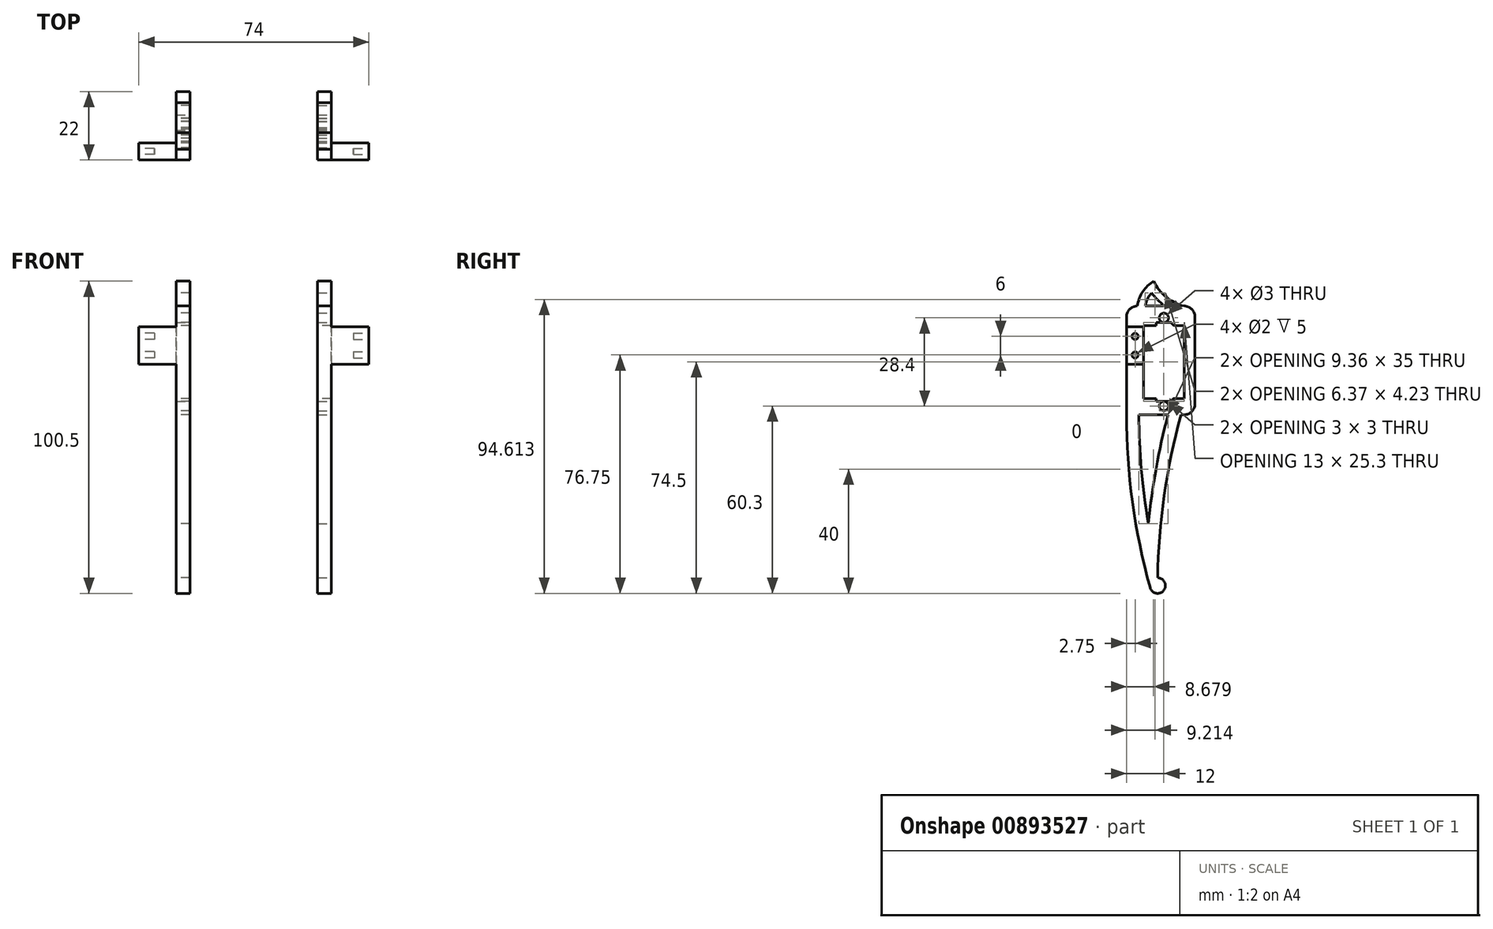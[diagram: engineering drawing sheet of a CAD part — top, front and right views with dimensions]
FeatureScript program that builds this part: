
annotation { "Feature Type Name" : "Feature", "Feature Type Description" : "" }
export const myFeature = defineFeature(function(context is Context, id is Id, definition is map)
    precondition{}
    {
        {
            var Q0;
            Q0=qCreatedBy(makeId("Right.planeOp"),FACE);
            var sketch = newSketch(context, id + "F0", { "sketchPlane" : qUnion([Q0])});
            skLineSegment(sketch, "E0.bottom", {"start": v(11, -17.5) * mm, "end": v(-11, -17.5) * mm});
            skLineSegment(sketch, "E0.top", {"start": v(11, 17.5) * mm, "end": v(-11, 17.5) * mm});
            skLineSegment(sketch, "E0.left", {"start": v(11, -17.5) * mm, "end": v(11, 17.5) * mm});
            skLineSegment(sketch, "E0.right", {"start": v(-11, -17.5) * mm, "end": v(-11, 17.5) * mm});
            skPoint(sketch, "E0.middle", {"position": v(0, 0) * mm});
            skSolve(sketch);
        }
        {
            var Q0;
            Q0 = qSketchRegion(id + "F0", true);
            extrude(context, id + "F1", {"entities" : qUnion([Q0]), "depth" : 4.5 * mm, "offsetDistance" : 25 * mm});
        }
        {
            var Q0;
            Q0=qCreatedBy(makeId("Right.planeOp"),FACE);
            var sketch = newSketch(context, id + "F2", { "sketchPlane" : qUnion([Q0])});
            skCircle(sketch, "E1", {"center": v(-1, -72.5) * mm, "radius": 2.5 * mm});
            skLineSegment(sketch, "E2.0", {"start": v(11, -17.5) * mm, "end": v(-11, -17.5) * mm});
            skArc(sketch, "E3", {"start": v(-11, -17.5) * mm, "mid": v(-9.1, -45.6) * mm, "end": v(-3.4, -73.17) * mm});
            skArc(sketch, "E4", {"start": v(6.5, -17.5) * mm, "mid": v(1.14, -43.52) * mm, "end": v(-1, -70) * mm});
            skLineSegment(sketch, "E5", {"start": v(-1, -70) * mm, "end": v(-1, -72.5) * mm, "construction": true});
            skArc(sketch, "E6.0", {"start": v(-7, -17.5) * mm, "mid": v(-6.24, -35.07) * mm, "end": v(-3.97, -52.5) * mm});
            skArc(sketch, "E7.0", {"start": v(2.36, -17.5) * mm, "mid": v(-1.51, -34.87) * mm, "end": v(-3.97, -52.5) * mm});
            skSolve(sketch);
        }
        {
            var Q0;
            {var subQ0=sQuery(id+"F2.wireOp",EDGE,"E3");Q0=makeQuery(id+"F2.imprint","IMPRINT",FACE,{"disambiguationData":[TD([[makeQuery(id+"F2.imprint","IMPRINT",EDGE,{"derivedFrom":subQ0}),1.0]])]});}
            var Q1;
            {var subQ0=sQuery(id+"F2.wireOp",EDGE,"E1");var subQ1=makeQuery(id+"F2.imprint","INTERSECT",VERTEX,{"derivedFrom":[subQ0,sQuery(id+"F2.wireOp",EDGE,"E3")]});Q1=makeQuery(id+"F2.imprint","IMPRINT",FACE,{"disambiguationData":[TD([[makeQuery(id+"F2.imprint","IMPRINT",EDGE,{"disambiguationData":[TD([[subQ1,1.0]])],"derivedFrom":subQ0}),1.0]])]});}
            var Q2;
            Q2=makeQuery(id+"F1.opExtrude","CAP_FACE",FACE,{"disambiguationData":[OSD([sQuery(id+"F0.wireOp",EDGE,"E0.bottom"),sQuery(id+"F0.wireOp",EDGE,"E0.top"),sQuery(id+"F0.wireOp",EDGE,"E0.left"),sQuery(id+"F0.wireOp",EDGE,"E0.right")])],"isStart":false});
            extrude(context, id + "F3", {"entities" : qUnion([Q0, Q1]), "operationType" : NewBodyOperationType.ADD, "endBound" : BoundingType.UP_TO_SURFACE, "depth" : 25 * mm, "endBoundEntityFace" : qUnion([Q2]), "offsetDistance" : 25 * mm});
        }
        {
            var Q0;
            Q0=makeQuery(id+"F1.opExtrude","SWEPT_EDGE",EDGE,{"disambiguationData":[OSD([sQuery(id+"F0.wireOp",EDGE,"E0.top"),sQuery(id+"F0.wireOp",EDGE,"E0.right")])]});
            var Q1;
            Q1=makeQuery(id+"F1.opExtrude","SWEPT_EDGE",EDGE,{"disambiguationData":[OSD([sQuery(id+"F0.wireOp",EDGE,"E0.top"),sQuery(id+"F0.wireOp",EDGE,"E0.left")])]});
            var Q2;
            Q2=makeQuery(id+"F1.opExtrude","SWEPT_EDGE",EDGE,{"disambiguationData":[OSD([sQuery(id+"F0.wireOp",EDGE,"E0.bottom"),sQuery(id+"F0.wireOp",EDGE,"E0.left")])]});
            fillet(context, id + "F4", {"entities" : qUnion([Q0, Q1, Q2]), "radius" : 3.5 * mm, "tangentPropagation" : true, "allowEdgeOverflow" : false});
        }
        {
            var Q0;
            Q0=qCreatedBy(makeId("Right.planeOp"),FACE);
            var sketch = newSketch(context, id + "F5", { "sketchPlane" : qUnion([Q0])});
            skLineSegment(sketch, "E8.0", {"start": v(7.5, 17.5) * mm, "end": v(-7.5, 17.5) * mm});
            skArc(sketch, "E9", {"start": v(-2.25, 25.5) * mm, "mid": v(1.7, 20.38) * mm, "end": v(7.5, 17.5) * mm});
            skArc(sketch, "E10", {"start": v(-2.25, 25.5) * mm, "mid": v(-5.8, 22.1) * mm, "end": v(-7.5, 17.5) * mm});
            skArc(sketch, "E11.0", {"start": v(-2.94, 21.73) * mm, "mid": v(-4.25, 19.76) * mm, "end": v(-4.97, 17.5) * mm});
            skArc(sketch, "E11.1", {"start": v(-2.94, 21.73) * mm, "mid": v(-0.96, 19.42) * mm, "end": v(1.4, 17.5) * mm});
            skSolve(sketch);
        }
        {
            var Q0;
            {var subQ1=sQuery(id+"F5.wireOp",EDGE,"E9");Q0=makeQuery(id+"F5.imprint","IMPRINT",FACE,{"disambiguationData":[TD([[makeQuery(id+"F5.imprint","IMPRINT",EDGE,{"derivedFrom":subQ1}),-1.0]])]});}
            var Q1;
            Q1=makeQuery(id+"F3.boolean.opBoolean","MERGE",FACE,{"derivedFrom":[makeQuery(id+"F1.opExtrude","CAP_FACE",FACE,{"disambiguationData":[OSD([sQuery(id+"F0.wireOp",EDGE,"E0.bottom"),sQuery(id+"F0.wireOp",EDGE,"E0.top"),sQuery(id+"F0.wireOp",EDGE,"E0.left"),sQuery(id+"F0.wireOp",EDGE,"E0.right")])],"isStart":false}),makeQuery(id+"F3.opExtrude","CAP_FACE",FACE,{"disambiguationData":[OSD([sQuery(id+"F2.wireOp",EDGE,"E1"),sQuery(id+"F2.wireOp",EDGE,"E2.0"),sQuery(id+"F2.wireOp",EDGE,"E3"),sQuery(id+"F2.wireOp",EDGE,"E4"),sQuery(id+"F2.wireOp",EDGE,"E6.0"),sQuery(id+"F2.wireOp",EDGE,"E7.0")])],"isStart":false})]});
            extrude(context, id + "F6", {"entities" : qUnion([Q0]), "operationType" : NewBodyOperationType.ADD, "endBound" : BoundingType.UP_TO_SURFACE, "depth" : 25 * mm, "endBoundEntityFace" : qUnion([Q1]), "offsetDistance" : 25 * mm});
        }
        {
            var Q0;
            Q0=makeQuery(id+"F6.boolean.opBoolean","MERGE",FACE,{"derivedFrom":[makeQuery(id+"F3.boolean.opBoolean","MERGE",FACE,{"derivedFrom":[makeQuery(id+"F1.opExtrude","CAP_FACE",FACE,{"disambiguationData":[OSD([sQuery(id+"F0.wireOp",EDGE,"E0.bottom"),sQuery(id+"F0.wireOp",EDGE,"E0.top"),sQuery(id+"F0.wireOp",EDGE,"E0.left"),sQuery(id+"F0.wireOp",EDGE,"E0.right")])],"isStart":true}),makeQuery(id+"F3.opExtrude","CAP_FACE",FACE,{"disambiguationData":[OSD([sQuery(id+"F2.wireOp",EDGE,"E1"),sQuery(id+"F2.wireOp",EDGE,"E2.0"),sQuery(id+"F2.wireOp",EDGE,"E3"),sQuery(id+"F2.wireOp",EDGE,"E4"),sQuery(id+"F2.wireOp",EDGE,"E6.0"),sQuery(id+"F2.wireOp",EDGE,"E7.0")])],"isStart":true})]}),makeQuery(id+"F6.opExtrude","CAP_FACE",FACE,{"disambiguationData":[OSD([sQuery(id+"F5.wireOp",EDGE,"E8.0"),sQuery(id+"F5.wireOp",EDGE,"E9"),sQuery(id+"F5.wireOp",EDGE,"E10"),sQuery(id+"F5.wireOp",EDGE,"E11.0"),sQuery(id+"F5.wireOp",EDGE,"E11.1")])],"isStart":true})]});
            var sketch = newSketch(context, id + "F7", { "sketchPlane" : qUnion([Q0])});
            skLineSegment(sketch, "E12.bottom", {"start": v(11, 10.75) * mm, "end": v(5.5, 10.75) * mm});
            skLineSegment(sketch, "E12.top", {"start": v(11, -1.25) * mm, "end": v(5.5, -1.25) * mm});
            skLineSegment(sketch, "E12.left", {"start": v(11, 10.75) * mm, "end": v(11, -1.25) * mm});
            skLineSegment(sketch, "E12.right", {"start": v(5.5, 10.75) * mm, "end": v(5.5, -1.25) * mm});
            skSolve(sketch);
        }
        {
            var Q0;
            Q0 = qSketchRegion(id + "F7", true);
            extrude(context, id + "F8", {"entities" : qUnion([Q0]), "operationType" : NewBodyOperationType.ADD, "depth" : 12 * mm, "offsetDistance" : 25 * mm});
        }
        {
            var Q0;
            Q0=makeQuery(id+"F6.boolean.opBoolean","MERGE",FACE,{"derivedFrom":[makeQuery(id+"F3.boolean.opBoolean","MERGE",FACE,{"derivedFrom":[makeQuery(id+"F1.opExtrude","CAP_FACE",FACE,{"disambiguationData":[OSD([sQuery(id+"F0.wireOp",EDGE,"E0.bottom"),sQuery(id+"F0.wireOp",EDGE,"E0.top"),sQuery(id+"F0.wireOp",EDGE,"E0.left"),sQuery(id+"F0.wireOp",EDGE,"E0.right")])],"isStart":true}),makeQuery(id+"F3.opExtrude","CAP_FACE",FACE,{"disambiguationData":[OSD([sQuery(id+"F2.wireOp",EDGE,"E1"),sQuery(id+"F2.wireOp",EDGE,"E2.0"),sQuery(id+"F2.wireOp",EDGE,"E3"),sQuery(id+"F2.wireOp",EDGE,"E4"),sQuery(id+"F2.wireOp",EDGE,"E6.0"),sQuery(id+"F2.wireOp",EDGE,"E7.0")])],"isStart":true})]}),makeQuery(id+"F6.opExtrude","CAP_FACE",FACE,{"disambiguationData":[OSD([sQuery(id+"F5.wireOp",EDGE,"E8.0"),sQuery(id+"F5.wireOp",EDGE,"E9"),sQuery(id+"F5.wireOp",EDGE,"E10"),sQuery(id+"F5.wireOp",EDGE,"E11.0"),sQuery(id+"F5.wireOp",EDGE,"E11.1")])],"isStart":true})]});
            var sketch = newSketch(context, id + "F9", { "sketchPlane" : qUnion([Q0])});
            skLineSegment(sketch, "E13.bottom", {"start": v(5.5, 11.25) * mm, "end": v(-7.5, 11.25) * mm});
            skLineSegment(sketch, "E13.top", {"start": v(5.5, -12.25) * mm, "end": v(-7.5, -12.25) * mm});
            skLineSegment(sketch, "E13.left", {"start": v(5.5, 11.25) * mm, "end": v(5.5, -12.25) * mm});
            skLineSegment(sketch, "E13.right", {"start": v(-7.5, 11.25) * mm, "end": v(-7.5, -12.25) * mm});
            skSolve(sketch);
        }
        {
            var Q0;
            Q0 = qSketchRegion(id + "F9", true);
            extrude(context, id + "F10", {"entities" : qUnion([Q0]), "operationType" : NewBodyOperationType.REMOVE, "oppositeDirection" : true, "depth" : 25 * mm, "offsetDistance" : 25 * mm});
        }
        {
            var Q0;
            Q0=makeQuery(id+"F6.boolean.opBoolean","MERGE",FACE,{"derivedFrom":[makeQuery(id+"F3.boolean.opBoolean","MERGE",FACE,{"derivedFrom":[makeQuery(id+"F1.opExtrude","CAP_FACE",FACE,{"disambiguationData":[OSD([sQuery(id+"F0.wireOp",EDGE,"E0.bottom"),sQuery(id+"F0.wireOp",EDGE,"E0.top"),sQuery(id+"F0.wireOp",EDGE,"E0.left"),sQuery(id+"F0.wireOp",EDGE,"E0.right")])],"isStart":true}),makeQuery(id+"F3.opExtrude","CAP_FACE",FACE,{"disambiguationData":[OSD([sQuery(id+"F2.wireOp",EDGE,"E1"),sQuery(id+"F2.wireOp",EDGE,"E2.0"),sQuery(id+"F2.wireOp",EDGE,"E3"),sQuery(id+"F2.wireOp",EDGE,"E4"),sQuery(id+"F2.wireOp",EDGE,"E6.0"),sQuery(id+"F2.wireOp",EDGE,"E7.0")])],"isStart":true})]}),makeQuery(id+"F6.opExtrude","CAP_FACE",FACE,{"disambiguationData":[OSD([sQuery(id+"F5.wireOp",EDGE,"E8.0"),sQuery(id+"F5.wireOp",EDGE,"E9"),sQuery(id+"F5.wireOp",EDGE,"E10"),sQuery(id+"F5.wireOp",EDGE,"E11.0"),sQuery(id+"F5.wireOp",EDGE,"E11.1")])],"isStart":true})]});
            var sketch = newSketch(context, id + "F11", { "sketchPlane" : qUnion([Q0])});
            skCircle(sketch, "E14", {"center": v(-1, 13.7) * mm, "radius": 1.5 * mm});
            skCircle(sketch, "E15", {"center": v(-1, -14.7) * mm, "radius": 1.5 * mm});
            skLineSegment(sketch, "E16", {"start": v(-1, 13.7) * mm, "end": v(-1, 11.25) * mm, "construction": true});
            skLineSegment(sketch, "E17", {"start": v(-1, -14.7) * mm, "end": v(-1, -12.25) * mm, "construction": true});
            skSolve(sketch);
        }
        {
            var Q0;
            Q0 = qSketchRegion(id + "F11", true);
            extrude(context, id + "F12", {"entities" : qUnion([Q0]), "operationType" : NewBodyOperationType.REMOVE, "oppositeDirection" : true, "depth" : 25 * mm, "offsetDistance" : 25 * mm});
        }
        {
            var Q0;
            Q0=makeQuery(id+"F8.opExtrude","CAP_FACE",FACE,{"disambiguationData":[OSD([sQuery(id+"F7.wireOp",EDGE,"E12.bottom"),sQuery(id+"F7.wireOp",EDGE,"E12.top"),sQuery(id+"F7.wireOp",EDGE,"E12.left"),sQuery(id+"F7.wireOp",EDGE,"E12.right")])],"isStart":false});
            var sketch = newSketch(context, id + "F13", { "sketchPlane" : qUnion([Q0])});
            skLineSegment(sketch, "E18", {"start": v(8.25, 10.75) * mm, "end": v(8.25, 7.75) * mm, "construction": true});
            skLineSegment(sketch, "E19", {"start": v(8.25, 7.75) * mm, "end": v(8.25, 1.75) * mm, "construction": true});
            skLineSegment(sketch, "E20", {"start": v(8.25, 1.75) * mm, "end": v(8.25, -1.25) * mm, "construction": true});
            skCircle(sketch, "E21", {"center": v(8.25, 7.75) * mm, "radius": 1 * mm});
            skCircle(sketch, "E22", {"center": v(8.25, 1.75) * mm, "radius": 1 * mm});
            skSolve(sketch);
        }
        {
            var Q0;
            Q0 = qSketchRegion(id + "F13", true);
            extrude(context, id + "F14", {"entities" : qUnion([Q0]), "operationType" : NewBodyOperationType.REMOVE, "oppositeDirection" : true, "depth" : 5 * mm, "offsetDistance" : 25 * mm});
        }
        {
            var Q0;
            Q0=qCreatedBy(makeId("Right.planeOp"),FACE);
            cPlane(context, id + "F15", {"entities" : qUnion([Q0]), "cplaneType" : CPlaneType.OFFSET, "offset" : 25 * mm, "width" : 150 * mm, "height" : 150 * mm});
        }
        {
            var Q0;
            Q0=makeQuery(id+"F1.opExtrude","SWEPT_BODY",BODY,{"disambiguationData":[OSD([sQuery(id+"F0.wireOp",EDGE,"E0.bottom"),sQuery(id+"F0.wireOp",EDGE,"E0.top"),sQuery(id+"F0.wireOp",EDGE,"E0.left"),sQuery(id+"F0.wireOp",EDGE,"E0.right")])]});
            var Q1;
            Q1=qCreatedBy(id+"F15.planeOp",FACE);
            mirror(context, id + "F16", {"entities" : qUnion([Q0]), "mirrorPlane" : qUnion([Q1])});
        }
        {
            var Q0;
            Q0=makeQuery(id+"F16.opPattern","COPY",FACE,{"derivedFrom":makeQuery(id+"F6.boolean.opBoolean","MERGE",FACE,{"derivedFrom":[makeQuery(id+"F3.boolean.opBoolean","MERGE",FACE,{"derivedFrom":[makeQuery(id+"F1.opExtrude","CAP_FACE",FACE,{"disambiguationData":[OSD([sQuery(id+"F0.wireOp",EDGE,"E0.bottom"),sQuery(id+"F0.wireOp",EDGE,"E0.top"),sQuery(id+"F0.wireOp",EDGE,"E0.left"),sQuery(id+"F0.wireOp",EDGE,"E0.right")])],"isStart":true}),makeQuery(id+"F3.opExtrude","CAP_FACE",FACE,{"disambiguationData":[OSD([sQuery(id+"F2.wireOp",EDGE,"E1"),sQuery(id+"F2.wireOp",EDGE,"E2.0"),sQuery(id+"F2.wireOp",EDGE,"E3"),sQuery(id+"F2.wireOp",EDGE,"E4"),sQuery(id+"F2.wireOp",EDGE,"E6.0"),sQuery(id+"F2.wireOp",EDGE,"E7.0")])],"isStart":true})]}),makeQuery(id+"F6.opExtrude","CAP_FACE",FACE,{"disambiguationData":[OSD([sQuery(id+"F5.wireOp",EDGE,"E8.0"),sQuery(id+"F5.wireOp",EDGE,"E9"),sQuery(id+"F5.wireOp",EDGE,"E10"),sQuery(id+"F5.wireOp",EDGE,"E11.0"),sQuery(id+"F5.wireOp",EDGE,"E11.1")])],"isStart":true})]}),"instanceName":"1"});
            var sketch = newSketch(context, id + "F17", { "sketchPlane" : qUnion([Q0])});
            skLineSegment(sketch, "E23.bottom", {"start": v(-1.5, 11.25) * mm, "end": v(3.5, 11.25) * mm});
            skLineSegment(sketch, "E23.top", {"start": v(-1.5, 12.15) * mm, "end": v(3.5, 12.15) * mm});
            skLineSegment(sketch, "E23.left", {"start": v(3.5, 11.25) * mm, "end": v(3.5, 12.15) * mm});
            skLineSegment(sketch, "E23.right", {"start": v(-1.5, 11.25) * mm, "end": v(-1.5, 12.15) * mm});
            skLineSegment(sketch, "E24.bottom", {"start": v(-1.5, -12.25) * mm, "end": v(3.5, -12.25) * mm});
            skLineSegment(sketch, "E24.top", {"start": v(-1.5, -13.15) * mm, "end": v(3.5, -13.15) * mm});
            skLineSegment(sketch, "E24.left", {"start": v(-1.5, -12.25) * mm, "end": v(-1.5, -13.15) * mm});
            skLineSegment(sketch, "E24.right", {"start": v(3.5, -12.25) * mm, "end": v(3.5, -13.15) * mm});
            skSolve(sketch);
        }
        {
            var Q0;
            Q0 = qSketchRegion(id + "F17", true);
            extrude(context, id + "F18", {"entities" : qUnion([Q0]), "operationType" : NewBodyOperationType.REMOVE, "oppositeDirection" : true, "depth" : 60 * mm, "offsetDistance" : 25 * mm});
        }
        {
            var Q0;
            {var subQ0=sQuery(id+"F9.wireOp",EDGE,"E13.bottom");var subQ1=sQuery(id+"F17.wireOp",EDGE,"E23.right");Q0=makeQuery(id+"F18.boolean.opBoolean","COPY",EDGE,{"disambiguationData":[topologyDisambiguationEdgeConnected([makeQuery(id+"F16.opPattern","COPY",FACE,{"derivedFrom":makeQuery(id+"F10.boolean.opBoolean","COPY",FACE,{"derivedFrom":makeQuery(id+"F10.opExtrude","SWEPT_FACE",FACE,{"disambiguationData":[OSD([subQ0])]})}),"instanceName":"1"})])],"derivedFrom":makeQuery(id+"F18.opExtrude","SWEPT_EDGE",EDGE,{"disambiguationData":[OSD([subQ0,sQuery(id+"F17.wireOp",EDGE,"E23.bottom"),subQ1])]})});}
            var Q1;
            {var subQ0=sQuery(id+"F9.wireOp",EDGE,"E13.bottom");var subQ1=sQuery(id+"F17.wireOp",EDGE,"E23.left");Q1=makeQuery(id+"F18.boolean.opBoolean","COPY",EDGE,{"disambiguationData":[topologyDisambiguationEdgeConnected([makeQuery(id+"F16.opPattern","COPY",FACE,{"derivedFrom":makeQuery(id+"F10.boolean.opBoolean","COPY",FACE,{"derivedFrom":makeQuery(id+"F10.opExtrude","SWEPT_FACE",FACE,{"disambiguationData":[OSD([subQ0])]})}),"instanceName":"1"})])],"derivedFrom":makeQuery(id+"F18.opExtrude","SWEPT_EDGE",EDGE,{"disambiguationData":[OSD([subQ0,sQuery(id+"F17.wireOp",EDGE,"E23.bottom"),subQ1])]})});}
            var Q2;
            {var subQ0=sQuery(id+"F9.wireOp",EDGE,"E13.bottom");var subQ1=sQuery(id+"F17.wireOp",EDGE,"E23.right");Q2=makeQuery(id+"F18.boolean.opBoolean","COPY",EDGE,{"disambiguationData":[topologyDisambiguationEdgeConnected([makeQuery(id+"F10.boolean.opBoolean","COPY",FACE,{"derivedFrom":makeQuery(id+"F10.opExtrude","SWEPT_FACE",FACE,{"disambiguationData":[OSD([subQ0])]})})])],"derivedFrom":makeQuery(id+"F18.opExtrude","SWEPT_EDGE",EDGE,{"disambiguationData":[OSD([subQ0,sQuery(id+"F17.wireOp",EDGE,"E23.bottom"),subQ1])]})});}
            var Q3;
            {var subQ0=sQuery(id+"F9.wireOp",EDGE,"E13.bottom");var subQ1=sQuery(id+"F17.wireOp",EDGE,"E23.left");Q3=makeQuery(id+"F18.boolean.opBoolean","COPY",EDGE,{"disambiguationData":[topologyDisambiguationEdgeConnected([makeQuery(id+"F10.boolean.opBoolean","COPY",FACE,{"derivedFrom":makeQuery(id+"F10.opExtrude","SWEPT_FACE",FACE,{"disambiguationData":[OSD([subQ0])]})})])],"derivedFrom":makeQuery(id+"F18.opExtrude","SWEPT_EDGE",EDGE,{"disambiguationData":[OSD([subQ0,sQuery(id+"F17.wireOp",EDGE,"E23.bottom"),subQ1])]})});}
            var Q4;
            {var subQ0=sQuery(id+"F9.wireOp",EDGE,"E13.top");var subQ1=sQuery(id+"F17.wireOp",EDGE,"E24.right");Q4=makeQuery(id+"F18.boolean.opBoolean","COPY",EDGE,{"disambiguationData":[topologyDisambiguationEdgeConnected([makeQuery(id+"F10.boolean.opBoolean","COPY",FACE,{"derivedFrom":makeQuery(id+"F10.opExtrude","SWEPT_FACE",FACE,{"disambiguationData":[OSD([subQ0])]})})])],"derivedFrom":makeQuery(id+"F18.opExtrude","SWEPT_EDGE",EDGE,{"disambiguationData":[OSD([subQ0,sQuery(id+"F17.wireOp",EDGE,"E24.bottom"),subQ1])]})});}
            var Q5;
            {var subQ0=sQuery(id+"F9.wireOp",EDGE,"E13.top");var subQ1=sQuery(id+"F17.wireOp",EDGE,"E24.left");Q5=makeQuery(id+"F18.boolean.opBoolean","COPY",EDGE,{"disambiguationData":[topologyDisambiguationEdgeConnected([makeQuery(id+"F10.boolean.opBoolean","COPY",FACE,{"derivedFrom":makeQuery(id+"F10.opExtrude","SWEPT_FACE",FACE,{"disambiguationData":[OSD([subQ0])]})})])],"derivedFrom":makeQuery(id+"F18.opExtrude","SWEPT_EDGE",EDGE,{"disambiguationData":[OSD([subQ0,sQuery(id+"F17.wireOp",EDGE,"E24.bottom"),subQ1])]})});}
            var Q6;
            {var subQ0=sQuery(id+"F9.wireOp",EDGE,"E13.top");var subQ1=sQuery(id+"F17.wireOp",EDGE,"E24.left");Q6=makeQuery(id+"F18.boolean.opBoolean","COPY",EDGE,{"disambiguationData":[topologyDisambiguationEdgeConnected([makeQuery(id+"F16.opPattern","COPY",FACE,{"derivedFrom":makeQuery(id+"F10.boolean.opBoolean","COPY",FACE,{"derivedFrom":makeQuery(id+"F10.opExtrude","SWEPT_FACE",FACE,{"disambiguationData":[OSD([subQ0])]})}),"instanceName":"1"})])],"derivedFrom":makeQuery(id+"F18.opExtrude","SWEPT_EDGE",EDGE,{"disambiguationData":[OSD([subQ0,sQuery(id+"F17.wireOp",EDGE,"E24.bottom"),subQ1])]})});}
            var Q7;
            {var subQ0=sQuery(id+"F9.wireOp",EDGE,"E13.top");var subQ1=sQuery(id+"F17.wireOp",EDGE,"E24.right");Q7=makeQuery(id+"F18.boolean.opBoolean","COPY",EDGE,{"disambiguationData":[topologyDisambiguationEdgeConnected([makeQuery(id+"F16.opPattern","COPY",FACE,{"derivedFrom":makeQuery(id+"F10.boolean.opBoolean","COPY",FACE,{"derivedFrom":makeQuery(id+"F10.opExtrude","SWEPT_FACE",FACE,{"disambiguationData":[OSD([subQ0])]})}),"instanceName":"1"})])],"derivedFrom":makeQuery(id+"F18.opExtrude","SWEPT_EDGE",EDGE,{"disambiguationData":[OSD([subQ0,sQuery(id+"F17.wireOp",EDGE,"E24.bottom"),subQ1])]})});}
            fillet(context, id + "F19", {"entities" : qUnion([Q0, Q1, Q2, Q3, Q4, Q5, Q6, Q7]), "tangentPropagation" : true, "radius" : 1 * mm, "defaultsChanged" : true, "vertexSettings" : [], "allowEdgeOverflow" : false});
        }
    });
